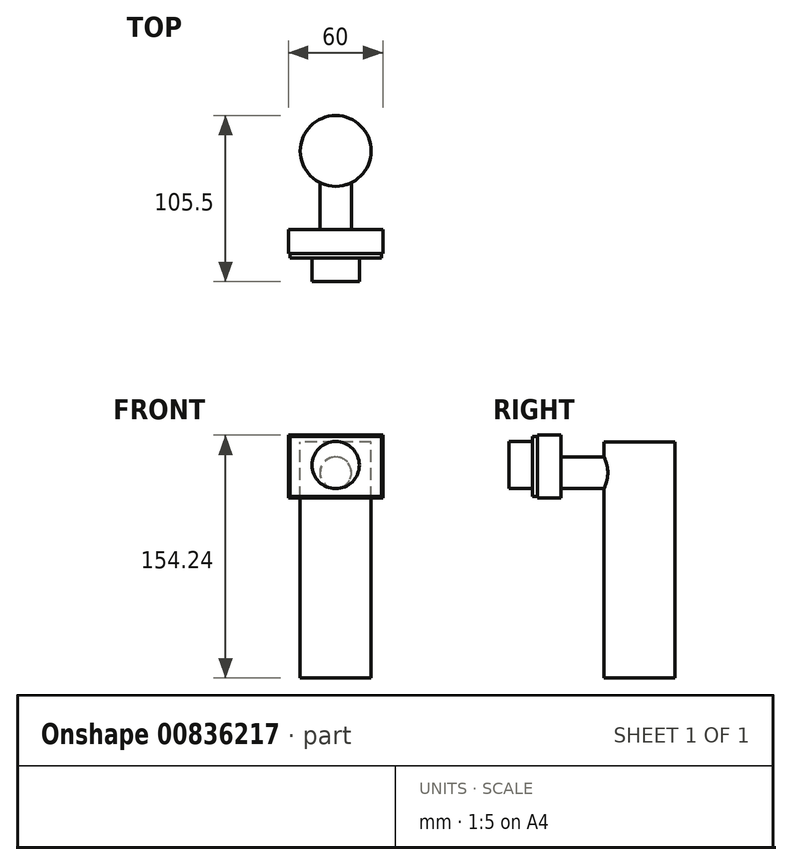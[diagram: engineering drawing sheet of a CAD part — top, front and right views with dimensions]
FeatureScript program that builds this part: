
annotation { "Feature Type Name" : "Feature", "Feature Type Description" : "" }
export const myFeature = defineFeature(function(context is Context, id is Id, definition is map)
    precondition{}
    {
        {
            var Q0;
            Q0=qCreatedBy(makeId("Top.planeOp"),FACE);
            var sketch = newSketch(context, id + "F0", { "sketchPlane" : qUnion([Q0])});
            skCircle(sketch, "E0", {"center": v(0, 0) * mm, "radius": 22.5 * mm});
            skSolve(sketch);
        }
        {
            var Q0;
            Q0=qCreatedBy(makeId("Front.planeOp"),FACE);
            var sketch = newSketch(context, id + "F1", { "sketchPlane" : qUnion([Q0])});
            skLineSegment(sketch, "E1", {"start": v(0, 0) * mm, "end": v(0, 150) * mm});
            skSolve(sketch);
        }
        {
            var Q0;
            Q0=qCreatedBy(makeId("Front.planeOp"),FACE);
            var sketch = newSketch(context, id + "F2", { "sketchPlane" : qUnion([Q0])});
            skCircle(sketch, "E2", {"center": v(0, 130.39) * mm, "radius": 10 * mm});
            skSolve(sketch);
        }
        {
            var Q0;
            Q0=makeQuery(id+"F2.imprint","IMPRINT",FACE,{"disambiguationData":[TD([[makeQuery(id+"F2.imprint","IMPRINT",EDGE,{"derivedFrom":sQuery(id+"F2.wireOp",EDGE,"E2")}),1.0]])]});
            extrude(context, id + "F3", {"entities" : qUnion([Q0]), "depth" : 50 * mm, "offsetDistance" : 25 * mm});
        }
        {
            var Q0;
            Q0=qCreatedBy(makeId("Front.planeOp"),FACE);
            cPlane(context, id + "F4", {"entities" : qUnion([Q0]), "cplaneType" : CPlaneType.OFFSET, "offset" : 50 * mm, "width" : 150 * mm, "height" : 150 * mm});
        }
        {
            var Q0;
            Q0=qCreatedBy(id+"F4.planeOp",FACE);
            var sketch = newSketch(context, id + "F5", { "sketchPlane" : qUnion([Q0])});
            skLineSegment(sketch, "E3.bottom", {"start": v(-30, 154.24) * mm, "end": v(30, 154.24) * mm});
            skLineSegment(sketch, "E3.top", {"start": v(-30, 114.24) * mm, "end": v(30, 114.24) * mm});
            skLineSegment(sketch, "E3.left", {"start": v(-30, 154.24) * mm, "end": v(-30, 114.24) * mm});
            skLineSegment(sketch, "E3.right", {"start": v(30, 154.24) * mm, "end": v(30, 114.24) * mm});
            skSolve(sketch);
        }
        {
            var Q0;
            Q0=makeQuery(id+"F5.imprint","IMPRINT",FACE,{"disambiguationData":[TD([[makeQuery(id+"F5.imprint","IMPRINT",EDGE,{"derivedFrom":sQuery(id+"F5.wireOp",EDGE,"E3.bottom")}),-1.0]])]});
            extrude(context, id + "F6", {"entities" : qUnion([Q0]), "operationType" : NewBodyOperationType.ADD, "depth" : 15 * mm, "offsetDistance" : 25 * mm});
        }
        {
            var Q0;
            Q0=makeQuery(id+"F0.imprint","IMPRINT",FACE,{"disambiguationData":[TD([[makeQuery(id+"F0.imprint","IMPRINT",EDGE,{"derivedFrom":sQuery(id+"F0.wireOp",EDGE,"E0")}),1.0]])]});
            var Q1;
            Q1=sQuery(id+"F1.wireOp",EDGE,"E1");
            sweep(context, id + "F7", {"operationType" : NewBodyOperationType.ADD, "profiles" : qUnion([Q0]), "path" : qUnion([Q1])});
        }
        {
            var Q0;
            Q0=makeQuery(id+"F6.opExtrude","CAP_FACE",FACE,{"disambiguationData":[OSD([sQuery(id+"F5.wireOp",EDGE,"E3.bottom"),sQuery(id+"F5.wireOp",EDGE,"E3.top"),sQuery(id+"F5.wireOp",EDGE,"E3.left"),sQuery(id+"F5.wireOp",EDGE,"E3.right")])],"isStart":false});
            var sketch = newSketch(context, id + "F8", { "sketchPlane" : qUnion([Q0])});
            skLineSegment(sketch, "E4.bottom", {"start": v(-29, 153.24) * mm, "end": v(29, 153.24) * mm});
            skLineSegment(sketch, "E4.top", {"start": v(-29, 115.24) * mm, "end": v(29, 115.24) * mm});
            skLineSegment(sketch, "E4.left", {"start": v(-29, 153.24) * mm, "end": v(-29, 115.24) * mm});
            skLineSegment(sketch, "E4.right", {"start": v(29, 153.24) * mm, "end": v(29, 115.24) * mm});
            skSolve(sketch);
        }
        {
            var Q0;
            Q0=makeQuery(id+"F8.imprint","IMPRINT",FACE,{"disambiguationData":[TD([[makeQuery(id+"F8.imprint","IMPRINT",EDGE,{"derivedFrom":sQuery(id+"F8.wireOp",EDGE,"E4.bottom")}),-1.0]])]});
            extrude(context, id + "F9", {"entities" : qUnion([Q0]), "operationType" : NewBodyOperationType.ADD, "depth" : 3 * mm, "offsetDistance" : 25 * mm});
        }
        {
            var Q0;
            Q0=makeQuery(id+"F9.opExtrude","CAP_FACE",FACE,{"disambiguationData":[OSD([sQuery(id+"F8.wireOp",EDGE,"E4.bottom"),sQuery(id+"F8.wireOp",EDGE,"E4.top"),sQuery(id+"F8.wireOp",EDGE,"E4.left"),sQuery(id+"F8.wireOp",EDGE,"E4.right")])],"isStart":false});
            var sketch = newSketch(context, id + "F10", { "sketchPlane" : qUnion([Q0])});
            skCircle(sketch, "E5", {"center": v(0, 135.24) * mm, "radius": 15 * mm});
            skSolve(sketch);
        }
        {
            var Q0;
            Q0=makeQuery(id+"F10.imprint","IMPRINT",FACE,{"disambiguationData":[TD([[makeQuery(id+"F10.imprint","IMPRINT",EDGE,{"derivedFrom":sQuery(id+"F10.wireOp",EDGE,"E5")}),1.0]])]});
            extrude(context, id + "F11", {"entities" : qUnion([Q0]), "operationType" : NewBodyOperationType.ADD, "depth" : 15 * mm, "offsetDistance" : 25 * mm});
        }
    });
